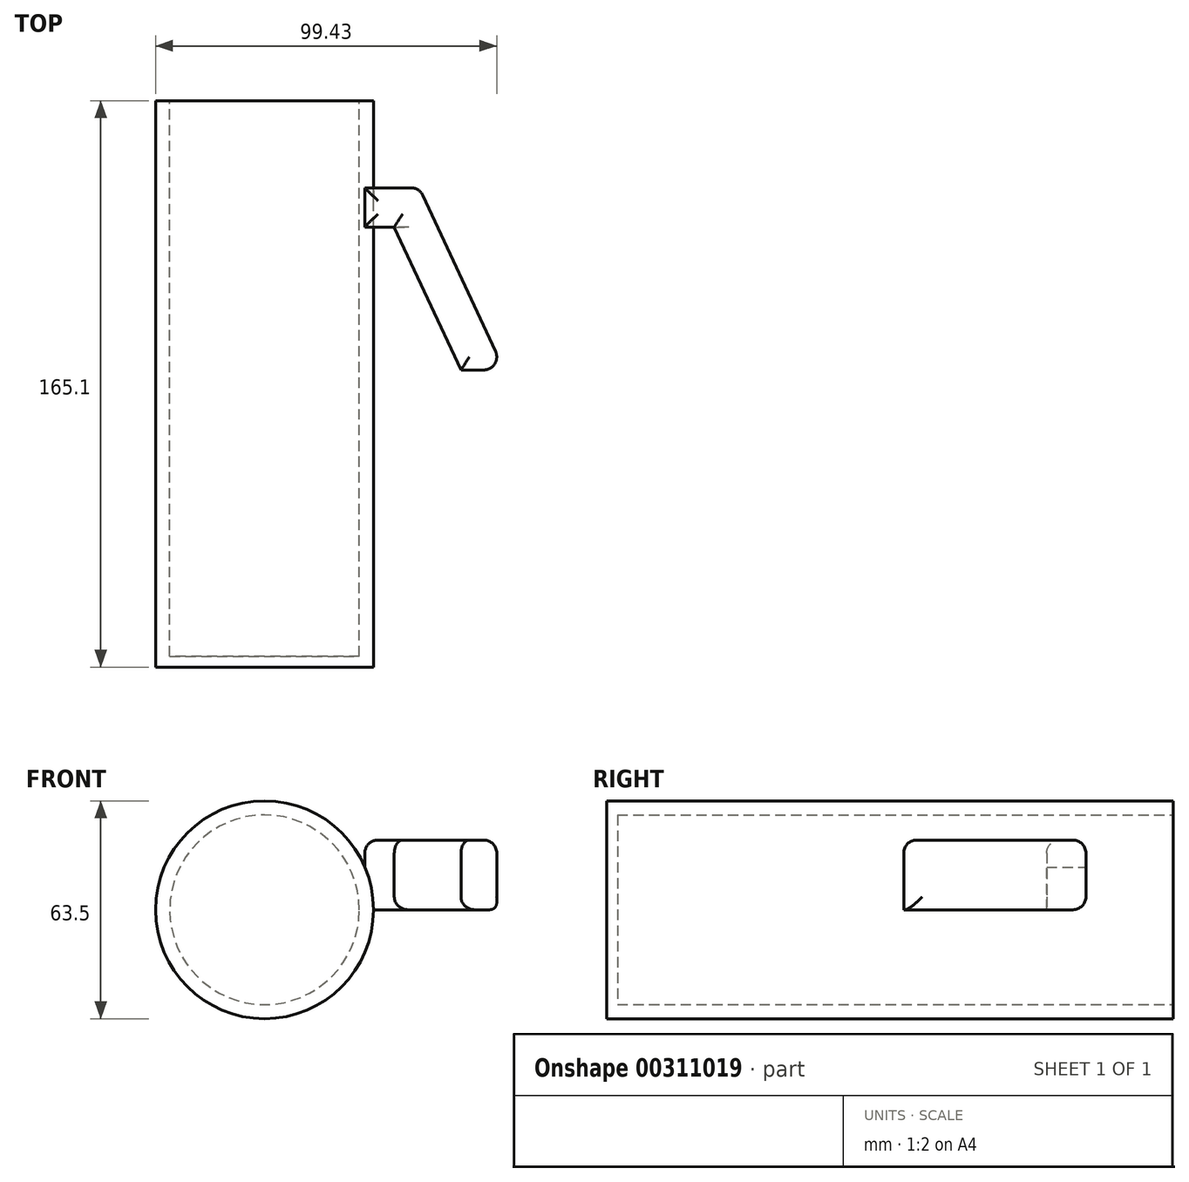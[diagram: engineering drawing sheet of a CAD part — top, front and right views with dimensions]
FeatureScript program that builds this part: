
annotation { "Feature Type Name" : "Feature", "Feature Type Description" : "" }
export const myFeature = defineFeature(function(context is Context, id is Id, definition is map)
    precondition{}
    {
        {
            var Q0;
            Q0=qCreatedBy(makeId("Front.planeOp"),FACE);
            var sketch = newSketch(context, id + "F0", { "sketchPlane" : qUnion([Q0])});
            skCircle(sketch, "E0", {"center": v(0, 0) * mm, "radius": 31.75 * mm});
            skCircle(sketch, "E1", {"center": v(0, 0) * mm, "radius": 28.58 * mm});
            skSolve(sketch);
        }
        {
            var Q0;
            Q0 = qSketchRegion(id + "F0", true);
            var Q1;
            Q1=makeQuery(id+"F0.imprint","IMPRINT",FACE,{"disambiguationData":[TD([[makeQuery(id+"F0.imprint","IMPRINT",EDGE,{"derivedFrom":sQuery(id+"F0.wireOp",EDGE,"E1")}),1.0]])]});
            extrude(context, id + "F1", {"entities" : qUnion([Q0, Q1]), "depth" : 165.1 * mm});
        }
        {
            var Q0;
            Q0=qCreatedBy(makeId("Top.planeOp"),FACE);
            var sketch = newSketch(context, id + "F2", { "sketchPlane" : qUnion([Q0])});
            skLineSegment(sketch, "E2", {"start": v(29.21, -25.4) * mm, "end": v(45.09, -25.4) * mm});
            skLineSegment(sketch, "E3", {"start": v(45.09, -25.4) * mm, "end": v(69.85, -78.5) * mm});
            skLineSegment(sketch, "E4", {"start": v(69.85, -78.5) * mm, "end": v(57.24, -78.5) * mm});
            skLineSegment(sketch, "E5", {"start": v(57.24, -78.5) * mm, "end": v(37.8, -36.83) * mm});
            skLineSegment(sketch, "E6", {"start": v(37.8, -36.83) * mm, "end": v(29.21, -36.83) * mm});
            skLineSegment(sketch, "E7", {"start": v(29.21, -36.83) * mm, "end": v(29.21, -25.4) * mm});
            skLineSegment(sketch, "E8.0.0", {"start": v(-31.75, 0) * mm, "end": v(31.75, 0) * mm});
            skSolve(sketch);
        }
        {
            var Q0;
            Q0=makeQuery(id+"F2.imprint","IMPRINT",FACE,{"disambiguationData":[TD([[makeQuery(id+"F2.imprint","IMPRINT",EDGE,{"derivedFrom":sQuery(id+"F2.wireOp",EDGE,"E2")}),-1.0]])]});
            extrude(context, id + "F3", {"entities" : qUnion([Q0]), "operationType" : NewBodyOperationType.ADD, "depth" : 20.32 * mm});
        }
        {
            var Q0;
            Q0=makeQuery(id+"F3.opExtrude","SWEPT_FACE",FACE,{"disambiguationData":[OSD([sQuery(id+"F2.wireOp",EDGE,"E3")])]});
            var Q1;
            Q1=makeQuery(id+"F3.opExtrude","CAP_FACE",FACE,{"disambiguationData":[OSD([sQuery(id+"F2.wireOp",EDGE,"E2"),sQuery(id+"F2.wireOp",EDGE,"E3"),sQuery(id+"F2.wireOp",EDGE,"E4"),sQuery(id+"F2.wireOp",EDGE,"E5"),sQuery(id+"F2.wireOp",EDGE,"E6"),sQuery(id+"F2.wireOp",EDGE,"E7")])],"isStart":false});
            var Q2;
            Q2=makeQuery(id+"F3.opExtrude","CAP_EDGE",EDGE,{"disambiguationData":[OSD([sQuery(id+"F2.wireOp",EDGE,"E5")])],"isStart":true});
            var Q3;
            Q3=makeQuery(id+"F3.opExtrude","CAP_EDGE",EDGE,{"disambiguationData":[OSD([sQuery(id+"F2.wireOp",EDGE,"E2")])],"isStart":true});
            fillet(context, id + "F4", {"entities" : qUnion([Q0, Q1, Q2, Q3]), "radius" : 3.8 * mm, "tangentPropagation" : true, "allowEdgeOverflow" : false});
        }
        {
            var Q0;
            Q0=makeQuery(id+"F1.opExtrude","CAP_FACE",FACE,{"disambiguationData":[OSD([sQuery(id+"F0.wireOp",EDGE,"E0")])],"isStart":true});
            var sketch = newSketch(context, id + "F5", { "sketchPlane" : qUnion([Q0])});
            skCircle(sketch, "E9", {"center": v(0, 0) * mm, "radius": 27.64 * mm});
            skSolve(sketch);
        }
        {
            var Q0;
            Q0 = qSketchRegion(id + "F5", true);
            extrude(context, id + "F6", {"entities" : qUnion([Q0]), "operationType" : NewBodyOperationType.REMOVE, "oppositeDirection" : true, "depth" : 161.92 * mm});
        }
    });
